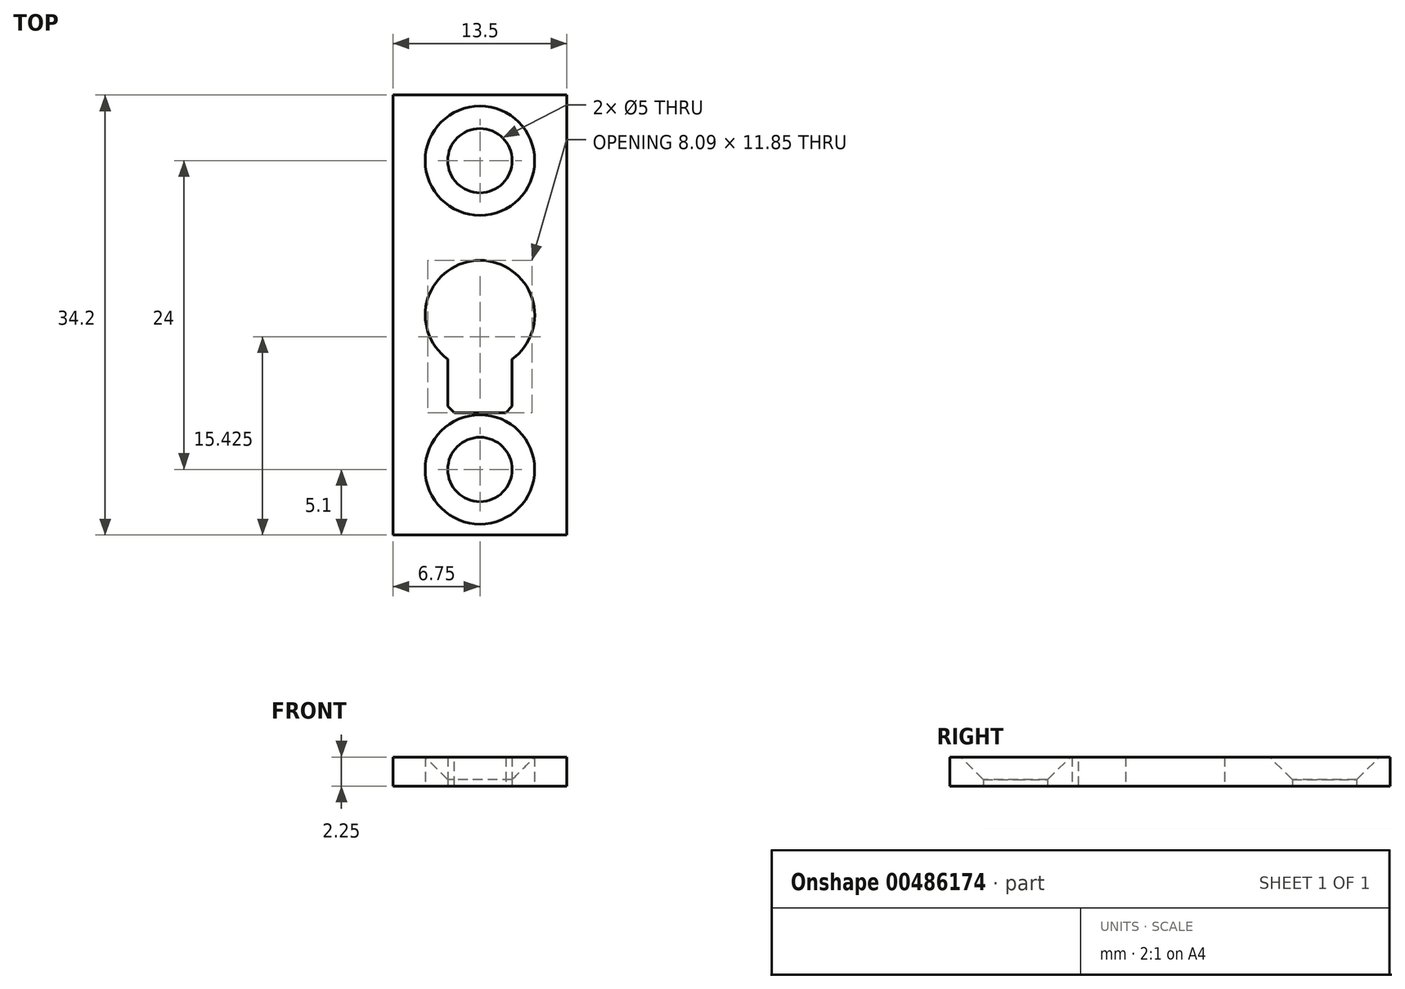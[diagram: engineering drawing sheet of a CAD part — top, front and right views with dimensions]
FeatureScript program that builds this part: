
annotation { "Feature Type Name" : "Feature", "Feature Type Description" : "" }
export const myFeature = defineFeature(function(context is Context, id is Id, definition is map)
    precondition{}
    {
        {
            var Q0;
            Q0=qCreatedBy(makeId("Top.planeOp"),FACE);
            var sketch = newSketch(context, id + "F0", { "sketchPlane" : qUnion([Q0])});
            skLineSegment(sketch, "E0.bottom", {"start": v(6.75, 17.1) * mm, "end": v(-6.75, 17.1) * mm});
            skLineSegment(sketch, "E0.top", {"start": v(6.75, -17.1) * mm, "end": v(-6.75, -17.1) * mm});
            skLineSegment(sketch, "E0.left", {"start": v(6.75, 17.1) * mm, "end": v(6.75, -17.1) * mm});
            skLineSegment(sketch, "E0.right", {"start": v(-6.75, 17.1) * mm, "end": v(-6.75, -17.1) * mm});
            skPoint(sketch, "E0.middle", {"position": v(0, 0) * mm});
            skLineSegment(sketch, "E1", {"start": v(0, 0) * mm, "end": v(0, 12) * mm});
            skLineSegment(sketch, "E2", {"start": v(0, 0) * mm, "end": v(0, -12) * mm});
            skCircle(sketch, "E3", {"center": v(0, 12) * mm, "radius": 2.5 * mm});
            skCircle(sketch, "E4", {"center": v(0, -12) * mm, "radius": 2.5 * mm});
            skCircle(sketch, "E5", {"center": v(0, 0) * mm, "radius": 4.25 * mm});
            skLineSegment(sketch, "E6", {"start": v(0, 0) * mm, "end": v(0, -7.6) * mm});
            skLineSegment(sketch, "E7", {"start": v(-2.5, -7.6) * mm, "end": v(-2.5, -3.44) * mm});
            skLineSegment(sketch, "E8", {"start": v(2.5, -7.6) * mm, "end": v(2.5, -3.44) * mm});
            skLineSegment(sketch, "E9", {"start": v(0, -7.6) * mm, "end": v(-2.5, -7.6) * mm});
            skLineSegment(sketch, "E10", {"start": v(0, -7.6) * mm, "end": v(2.5, -7.6) * mm});
            skSolve(sketch);
        }
        {
            var Q0;
            Q0 = qSketchRegion(id + "F0", true);
            extrude(context, id + "F1", {"entities" : qUnion([Q0]), "depth" : 2.25 * mm});
        }
        {
            var Q0;
            Q0=makeQuery(id+"F1.opExtrude","SWEPT_EDGE",EDGE,{"disambiguationData":[OSD([sQuery(id+"F0.wireOp",EDGE,"E7"),sQuery(id+"F0.wireOp",EDGE,"E9")])]});
            var Q1;
            Q1=makeQuery(id+"F1.opExtrude","SWEPT_EDGE",EDGE,{"disambiguationData":[OSD([sQuery(id+"F0.wireOp",EDGE,"E8"),sQuery(id+"F0.wireOp",EDGE,"E10")])]});
            chamfer(context, id + "F2", {"entities" : qUnion([Q0, Q1]), "width" : .5 * mm, "tangentPropagation" : true});
        }
        {
            var Q0;
            Q0=makeQuery(id+"F1.opExtrude","CAP_EDGE",EDGE,{"disambiguationData":[OSD([sQuery(id+"F0.wireOp",EDGE,"E4")])],"isStart":false});
            var Q1;
            Q1=makeQuery(id+"F1.opExtrude","CAP_EDGE",EDGE,{"disambiguationData":[OSD([sQuery(id+"F0.wireOp",EDGE,"E3")])],"isStart":false});
            chamfer(context, id + "F3", {"entities" : qUnion([Q0, Q1]), "width" : 1.75 * mm, "tangentPropagation" : true});
        }
    });
